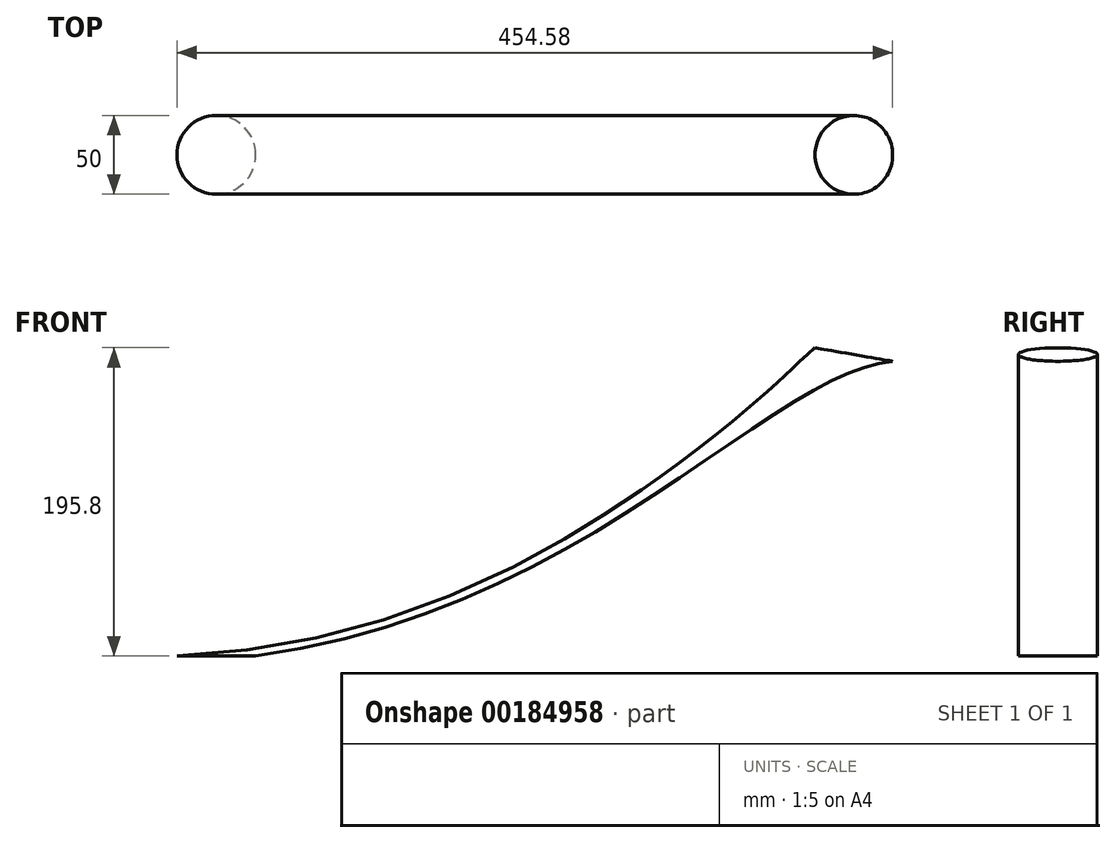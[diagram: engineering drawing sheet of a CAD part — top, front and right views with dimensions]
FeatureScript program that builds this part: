
annotation { "Feature Type Name" : "Feature", "Feature Type Description" : "" }
export const myFeature = defineFeature(function(context is Context, id is Id, definition is map)
    precondition{}
    {
        {
            var Q0;
            Q0=qCreatedBy(makeId("Top.planeOp"),FACE);
            var sketch = newSketch(context, id + "F0", { "sketchPlane" : qUnion([Q0])});
            skCircle(sketch, "E0", {"center": v(-424.8, 0) * mm, "radius": 25 * mm});
            skSolve(sketch);
        }
        {
            var Q0;
            Q0=qCreatedBy(makeId("Front.planeOp"),FACE);
            var sketch = newSketch(context, id + "F1", { "sketchPlane" : qUnion([Q0])});
            skFitSpline(sketch, "E1", {"points": [v(-397.24, 26.25) * mm, v(11.82, 212.6) * mm], "startDerivative": vector(640.4, 96.88) * mm, "endDerivative": vector(280.93, -6.45) * mm});
            skSolve(sketch);
        }
        {
            var Q0;
            Q0=makeQuery(id+"F0.imprint","IMPRINT",FACE,{"disambiguationData":[TD([[makeQuery(id+"F0.imprint","IMPRINT",EDGE,{"derivedFrom":sQuery(id+"F0.wireOp",EDGE,"E0")}),1.0]])]});
            var Q1;
            Q1=sQuery(id+"F1.wireOp",EDGE,"E1");
            sweep(context, id + "F2", {"profiles" : qUnion([Q0]), "path" : qUnion([Q1])});
        }
    });
